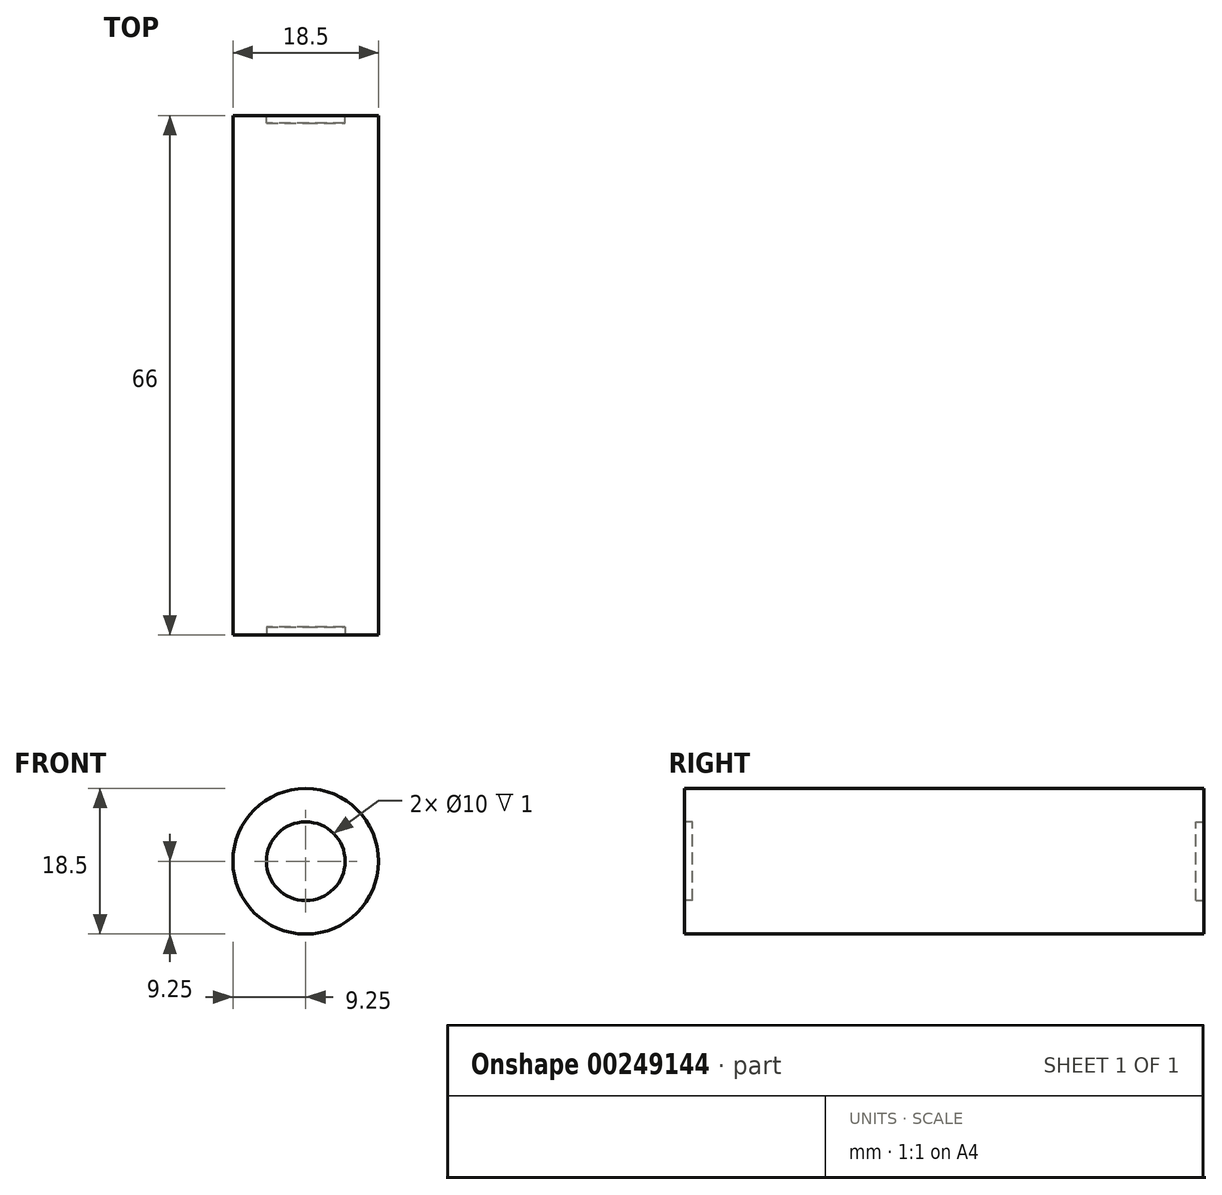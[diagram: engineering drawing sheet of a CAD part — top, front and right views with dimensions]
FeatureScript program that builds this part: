
annotation { "Feature Type Name" : "Feature", "Feature Type Description" : "" }
export const myFeature = defineFeature(function(context is Context, id is Id, definition is map)
    precondition{}
    {
        {
            var Q0;
            Q0=qCreatedBy(makeId("Front.planeOp"),FACE);
            var sketch = newSketch(context, id + "F0", { "sketchPlane" : qUnion([Q0])});
            skCircle(sketch, "E0", {"center": v(0, 0) * mm, "radius": 9.25 * mm});
            skSolve(sketch);
        }
        {
            var Q0;
            Q0=makeQuery(id+"F0.imprint","IMPRINT",FACE,{"disambiguationData":[TD([[makeQuery(id+"F0.imprint","IMPRINT",EDGE,{"derivedFrom":sQuery(id+"F0.wireOp",EDGE,"E0")}),1.0]])]});
            extrude(context, id + "F1", {"entities" : qUnion([Q0]), "depth" : 66 * mm});
        }
        {
            var Q0;
            Q0=qCreatedBy(makeId("Front.planeOp"),FACE);
            var sketch = newSketch(context, id + "F2", { "sketchPlane" : qUnion([Q0])});
            skCircle(sketch, "E1", {"center": v(0, 0) * mm, "radius": 5 * mm});
            skSolve(sketch);
        }
        {
            var Q0;
            Q0=makeQuery(id+"F2.imprint","IMPRINT",FACE,{"disambiguationData":[TD([[makeQuery(id+"F2.imprint","IMPRINT",EDGE,{"derivedFrom":sQuery(id+"F2.wireOp",EDGE,"E1")}),1.0]])]});
            extrude(context, id + "F3", {"entities" : qUnion([Q0]), "operationType" : NewBodyOperationType.REMOVE, "depth" : 1 * mm});
        }
        {
            var Q0;
            Q0=makeQuery(id+"F1.opExtrude","CAP_FACE",FACE,{"disambiguationData":[OSD([sQuery(id+"F0.wireOp",EDGE,"E0")])],"isStart":false});
            var sketch = newSketch(context, id + "F4", { "sketchPlane" : qUnion([Q0])});
            skCircle(sketch, "E2", {"center": v(0, 0) * mm, "radius": 5 * mm});
            skSolve(sketch);
        }
        {
            var Q0;
            Q0=makeQuery(id+"F4.imprint","IMPRINT",FACE,{"disambiguationData":[TD([[makeQuery(id+"F4.imprint","IMPRINT",EDGE,{"derivedFrom":sQuery(id+"F4.wireOp",EDGE,"E2")}),1.0]])]});
            extrude(context, id + "F5", {"entities" : qUnion([Q0]), "operationType" : NewBodyOperationType.REMOVE, "oppositeDirection" : true, "depth" : 1 * mm});
        }
    });
